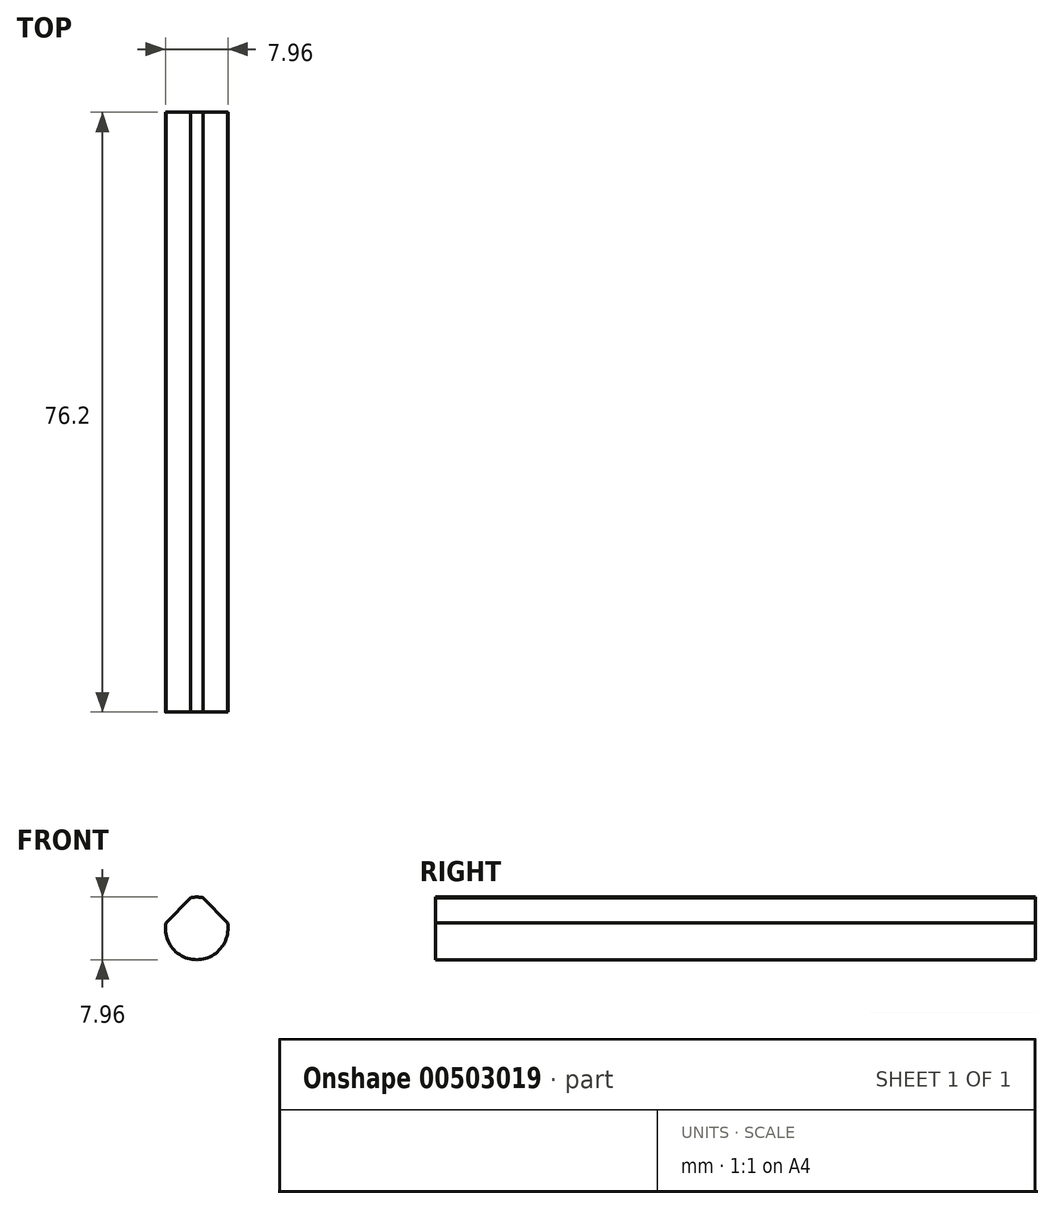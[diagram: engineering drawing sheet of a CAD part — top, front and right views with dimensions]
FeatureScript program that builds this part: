
annotation { "Feature Type Name" : "Feature", "Feature Type Description" : "" }
export const myFeature = defineFeature(function(context is Context, id is Id, definition is map)
    precondition{}
    {
        {
            var Q0;
            Q0=qCreatedBy(makeId("Front.planeOp"),FACE);
            var sketch = newSketch(context, id + "F0", { "sketchPlane" : qUnion([Q0])});
            skArc(sketch, "E0", {"start": v(0.8, 3.9) * mm, "mid": v(0, 3.98) * mm, "end": v(-0.8, 3.9) * mm});
            skArc(sketch, "E1", {"start": v(0, 3.98) * mm, "mid": v(0.4, 3.95) * mm, "end": v(0.8, 3.9) * mm});
            skLineSegment(sketch, "E2", {"start": v(-3.91, 0.71) * mm, "end": v(-0.8, 3.9) * mm});
            skLineSegment(sketch, "E3", {"start": v(0.8, 3.9) * mm, "end": v(3.91, 0.71) * mm});
            skArc(sketch, "E4.trimOffspring", {"start": v(-3.91, 0.71) * mm, "mid": v(0, -3.98) * mm, "end": v(3.91, 0.71) * mm});
            skSolve(sketch);
        }
        {
            var Q0;
            Q0=makeQuery(id+"F0.imprint","IMPRINT",FACE,{"disambiguationData":[TD([[makeQuery(id+"F0.imprint","IMPRINT",EDGE,{"derivedFrom":sQuery(id+"F0.wireOp",EDGE,"E0")}),1.0]])]});
            extrude(context, id + "F1", {"entities" : qUnion([Q0]), "depth" : 76.2 * mm});
        }
    });
